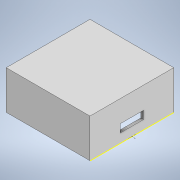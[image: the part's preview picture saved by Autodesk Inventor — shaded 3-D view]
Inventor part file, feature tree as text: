
AUTODESK INVENTOR PART (.ipt)
format: ipt  version: 2022 (Build 260153000, 153)  size: 131,584 bytes
history: native  units: in
note: dims shown in document units (in); Inventor stores cm internally (conversion verified against a paired STEP export)
features: sketch x5, extrude x4
ambient origin geometry x8: Origin, YZ Plane, XZ Plane, XY Plane, X Axis, Y Axis, Z Axis, Center Point
bodies: Solid1 (feature_tree)
feature tree (9):
  extrude  "Extrusion1"  Depth=0.2165in
  extrude  "Extrusion2"  Depth=0.2559in
  sketch  "Sketch5"  dims[d8=0.0787in d9=0.0in d10=0.2559in]
  extrude  "Extrusion3"  Depth=0.2559in
  extrude  "Extrusion4"  Depth=0.0394in
  sketch  "Sketch2"  dims[d2=0.2165in d3=0.2165in]
  sketch  "Sketch4"  dims[d6=0.2559in d7=0.2559in]
  sketch  "Sketch6"  dims[d11=0.0394in d12=0.0in d13=0.0945in]
  sketch  "Sketch7"  dims[d14=0.0472in d15=0.0394in d16=0.0197in d17=-0.2061in d18=0.0945in d19=0.0472in d20=0.0394in d21=0.0197in d22=-0.2061in]
